# Revit family: Toilet-Top_Spud-American_Standard-Madera-3043511.020
name_source: partatom
category: Plumbing Fixtures
units: mm (PartAtom-declared; Revit-internal decimal feet)

## family parameters
Always vertical = No
Cut with Voids When Loaded = No
OmniClass Number = 23.45.05.21.11.11
OmniClass Title = Water Operated Water Closets
Part Type = Normal
Room Calculation Point = No
Round Connector Dimension = Use Diameter
Shared = Yes
Work Plane-Based = Yes

## types (1)
- 3043511.020
    047007-0070A Inlet Spud (furnished with bowl) = Yes
    10" Rough In = No
    12" Rough In = Yes
    3043.001 Toilet Bowl = Yes
    481310-100 2 Bolt caps with retainers (furnished with bowl) = Yes
    6065.111 Flush Valve = Yes
    ADA Compliant = Yes
    Assembly Code = D2010110
    Bowl Shape = Elongated
    CW Connection = Yes
    CWFU = 5
    CalGreen Compliant = Yes
    Cold Water Connection Diameter = 1"
    Cold Water Connection Radius = 1/2"
    Cold Water Connection Width = 4 1/4"
    Cold Water Connection Width Constraint = 4 1/4"
    Compliance Certifications = Meets or Exceeds ASME A112.19.2-2008 / CSA B45.1-08 for Vitreous China Fixtures, ASSE 1037 & ANSI/ASME A112.19.2
    Default Elevation = 0"
    Description = Madera™ Chair Height Toilet System With Touchless Selectronic® Piston Flush Valve, 1.1 gpf/4.2 Lpf
    Finish = Vitreous China-American Standard-020-White
    Finish- Flush Valve = Metal-American Standard-002-Polished Chrome
    Flow Rate = 25gpm (94.6 L/min.)
    Flush Rate = 1.1 gpf (4.2 Lpf) to 1.6 gpf  (6.0 Lpf)
    HW Connection = No
    HWFU = 0
    Height = 33"
    Height- Bowl = 16 1/2"
    Installation Type = Floor Mounted
    Length = 28 1/4"
    Manufacturer = American Standard
    Material = Vitreous China-American Standard-020-White
    Model = 3043511.020
    Operating Pressure = 25 psi (flowing) - 80 psi (static)
    Price = Prices may vary. Please consult Manufacturer Representative for most up-to-date price list.
    Product Documentation Link = https://americanstandard.box.com
    Product Page URL = https://www.americanstandard-us.com
    Rough In Distance = 12"
    Seat - American Standard #5901.100 = No
    Seat - American Standard #5905.100 = No
    URL = http://www.americanstandard-us.com
    Valve Height = 16 1/2"
    Vent Connection = No
    WFU = 5
    Warranty Information = 8-year CR-P2 lithium battery installed in valve
    Waste Connection = Yes
    Waste Connection Diameter = 2 1/8"
    Waste Connection Radius = 1 1/16"
    Weight Lbs = 2,500 lbs (1,134 kg)
    Width = 14"

## geometry (parser evidence)
native form markers: Sweep x3
no freeform markers — native parametric forms only
